# Revit family: Deca_Bacia para caixa acoplada_Izy_P.115
name_source: partatom
category: Plumbing Fixtures
units: mm (PartAtom-declared; Revit-internal decimal feet)

## family parameters
Cut with Voids When Loaded = No
Host = Face
Part Type = Normal
Room Calculation Point = No
Round Connector Dimension = Use Radius
Shared = No

## types (1)
- P.115.17_Branco
    Acompanha o Produto = -
    Aprovado por = quattroD
    Atendimento ao Cliente = 0800-0117073
    Categoria = BACIAS E BIDES
    Composição Anel Vedação = Não Possui
    Composição Assento = -
    Composição Básica = Argila, feldspato, caulim, vidrados e corantes inorgânicos.
    Composição Componente = Não Possui
    Consumo = 6 lpf
    Cor Interna = -
    Cor Principal = Branco
    Cor Secundária = -
    Cores Componente = -
    Criado por = quattroD
    Código Pai = P.115
    Default Elevation = 0 m
    Description = Bacia para caixa acoplada
    Diâmetro Ponto de Esgoto = 0.1 m
    Diâmetro Água Fria = 0.02 m
    Informações Complementares = -
    Itens de Instalação = -
    Linha = Izy
    Manufacturer = Deca
    Material = Deca_Branco
    Model = P.115.17
    Norma = NBR-16727-1;NBR-16727-2;NBR9050
    Peso Líquido (Kg) = 14.93
    Pressão máx. funcionamento = -
    Pressão mín. Aquec. Acúmulo = -
    Pressão mín. Aquec. Passagem = -
    Pressão mín. funcionamento = -
    Raio Ponto de Esgoto = 0.05 m
    Raio Água Fria = 0.01 m
    Saída de Esgoto = Saída de Esgoto Vertical
    Segmento = Banheiro Competitivo
    Tipo de dispositivo economizador = -
    Tipo de mecanismo utilizado = -
    Tipo de rosca de entrada = -
    Tipo de rosca de saída = -
    URL = www.deca.com.br
    Vazão na Pressão máx. (L/min) = -
    Vazão na Pressão mín. (L/min) = -

## geometry (parser evidence)
native form markers: Sweep x5
no freeform markers — native parametric forms only
